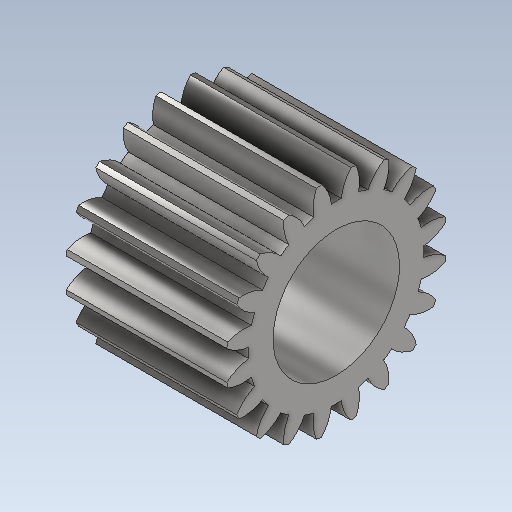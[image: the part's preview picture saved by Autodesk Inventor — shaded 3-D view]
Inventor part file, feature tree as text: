
AUTODESK INVENTOR PART (.ipt)
format: ipt  version: 2023 (Build 270158000, 158)  size: 317,952 bytes
history: native  units: in
note: dims shown in document units (in); Inventor stores cm internally (conversion verified against a paired STEP export)
features: other x3, sketch x2
ambient origin geometry x8: Origin, YZ Plane, XZ Plane, XY Plane, X Axis, Y Axis, Z Axis, Center Point
bodies: Solid1 (feature_tree)
feature tree (5):
  other  "CH-1-01-20T_Drive Gear.ipt"
  other  "Solid1::CH-1-01-20T_Drive Gear.ipt"
  other  "TaggingFeature1"
  sketch  "Sketch1"  dims[d0=0.3937in]
  sketch  "Sketch2"
